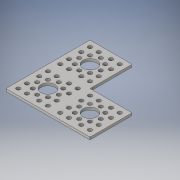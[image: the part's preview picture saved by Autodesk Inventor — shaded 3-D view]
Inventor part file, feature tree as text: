
AUTODESK INVENTOR PART (.ipt)
format: ipt  version: 2016 (Build 200138000, 138)  size: 218,624 bytes
history: native  units: in
note: dims shown in document units (in); Inventor stores cm internally (conversion verified against a paired STEP export)
features: fillet x1
ambient origin geometry x8: Origin, YZ Plane, XZ Plane, XY Plane, X Axis, Y Axis, Z Axis, Center Point
bodies: Solid1 (feature_tree)
feature tree (1):
  fillet  "Fillet1"  [1 undecoded]
note: 1 required parameter value undecoded (feature->parameter linkage not recoverable at this tier; creation-order binding heuristic only, values carry confidence <= 0.55)
